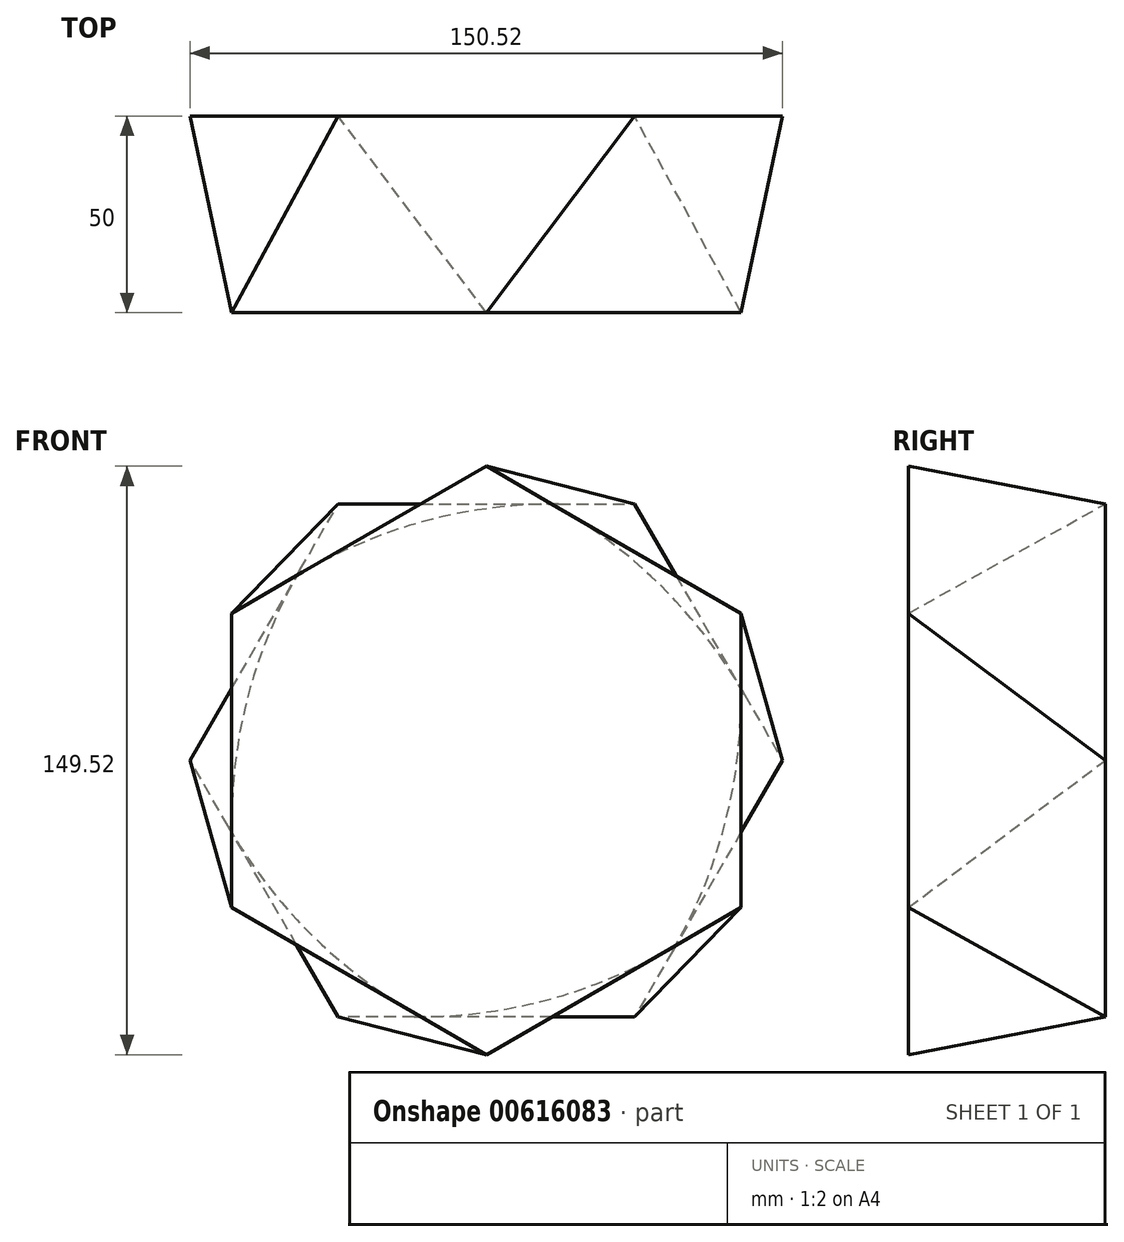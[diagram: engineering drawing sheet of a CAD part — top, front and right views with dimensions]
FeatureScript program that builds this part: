
annotation { "Feature Type Name" : "Feature", "Feature Type Description" : "" }
export const myFeature = defineFeature(function(context is Context, id is Id, definition is map)
    precondition{}
    {
        {
            var Q0;
            Q0=qCreatedBy(makeId("Front.planeOp"),FACE);
            var sketch = newSketch(context, id + "F0", { "sketchPlane" : qUnion([Q0])});
            skCircle(sketch, "E0.cCircle", {"center": v(0, 0) * mm, "radius": 75.26 * mm, "construction": true});
            skLineSegment(sketch, "E0.0", {"start": v(75.26, 0) * mm, "end": v(37.63, -65.18) * mm});
            skLineSegment(sketch, "E0.1", {"start": v(37.63, -65.18) * mm, "end": v(-37.63, -65.18) * mm});
            skLineSegment(sketch, "E0.2", {"start": v(-37.63, -65.18) * mm, "end": v(-75.26, 0) * mm});
            skLineSegment(sketch, "E0.3", {"start": v(-75.26, 0) * mm, "end": v(-37.63, 65.18) * mm});
            skLineSegment(sketch, "E0.4", {"start": v(-37.63, 65.18) * mm, "end": v(37.63, 65.18) * mm});
            skLineSegment(sketch, "E0.5", {"start": v(37.63, 65.18) * mm, "end": v(75.26, 0) * mm});
            skSolve(sketch);
        }
        {
            var Q0;
            Q0=qCreatedBy(makeId("Front.planeOp"),FACE);
            cPlane(context, id + "F1", {"entities" : qUnion([Q0]), "cplaneType" : CPlaneType.OFFSET, "offset" : 50 * mm, "width" : 150 * mm, "height" : 150 * mm});
        }
        {
            var Q0;
            Q0=qCreatedBy(id+"F1.planeOp",FACE);
            var sketch = newSketch(context, id + "F2", { "sketchPlane" : qUnion([Q0])});
            skCircle(sketch, "E1.cCircle", {"center": v(0, 0) * mm, "radius": 74.76 * mm, "construction": true});
            skLineSegment(sketch, "E1.0", {"start": v(0, -74.76) * mm, "end": v(-64.74, -37.38) * mm});
            skLineSegment(sketch, "E1.1", {"start": v(-64.74, -37.38) * mm, "end": v(-64.74, 37.38) * mm});
            skLineSegment(sketch, "E1.2", {"start": v(-64.74, 37.38) * mm, "end": v(0, 74.76) * mm});
            skLineSegment(sketch, "E1.3", {"start": v(0, 74.76) * mm, "end": v(64.74, 37.38) * mm});
            skLineSegment(sketch, "E1.4", {"start": v(64.74, 37.38) * mm, "end": v(64.74, -37.38) * mm});
            skLineSegment(sketch, "E1.5", {"start": v(64.74, -37.38) * mm, "end": v(0, -74.76) * mm});
            skSolve(sketch);
        }
        {
            var Q0;
            Q0=makeQuery(id+"F2.imprint","IMPRINT",FACE,{"disambiguationData":[TD([[makeQuery(id+"F2.imprint","IMPRINT",EDGE,{"derivedFrom":sQuery(id+"F2.wireOp",EDGE,"E1.0")}),-1.0]])]});
            var Q1;
            Q1=makeQuery(id+"F0.imprint","IMPRINT",FACE,{"disambiguationData":[TD([[makeQuery(id+"F0.imprint","IMPRINT",EDGE,{"derivedFrom":sQuery(id+"F0.wireOp",EDGE,"E0.0")}),-1.0]])]});
            loft(context, id + "F3", {"sheetProfilesArray" : [{ "sheetProfileEntities" : qUnion([Q0]) }, { "sheetProfileEntities" : qUnion([Q1]) }]});
        }
        {
            var Q0;
            Q0=qCreatedBy(makeId("Front.planeOp"),FACE);
            cPlane(context, id + "F4", {"entities" : qUnion([Q0]), "cplaneType" : CPlaneType.OFFSET, "offset" : 50 * mm, "oppositeDirection" : true, "width" : 150 * mm, "height" : 150 * mm});
        }
    });
